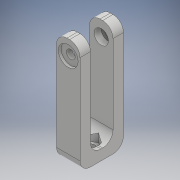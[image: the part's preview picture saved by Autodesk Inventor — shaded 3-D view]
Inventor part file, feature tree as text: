
AUTODESK INVENTOR PART (.ipt)
format: ipt  version: 2019 (Build 230136000, 136)  size: 224,768 bytes
history: native  units: mm
features: extrude x10, sketch x10, fillet x3, other x1, projected_geometry x1
ambient origin geometry x8: Origin, YZ Plane, XZ Plane, XY Plane, X Axis, Y Axis, Z Axis, Center Point
bodies: Body1 (feature_tree)
feature tree (25):
  other  "Sólido1"
  extrude  "Extrusión1"  Depth=6.0mm TaperAngle=0.0deg
  extrude  "Extrusión2"  Depth=115.0mm TaperAngle=0.0deg
  extrude  "Extrusión3"  Depth=17.0mm
  extrude  "Extrusión4"  Depth=27.0mm
  extrude  "Extrusión8"  Depth=12.0mm
  extrude  "Extrusión9"  Depth=10.0mm TaperAngle=0.0deg
  extrude  "Extrusión10"  Depth=2.5mm TaperAngle=0.0deg
  extrude  "Extrusión11"  Depth=3.0mm TaperAngle=0.0deg
  extrude  "Extrusión12"  Depth=8.0mm
  extrude  "Extrusión13"  Depth=12.0mm
  fillet  "Empalme4"  Radius=8.0mm
  fillet  "Empalme5"  Radius=16.0mm
  fillet  "Empalme6"  Radius=12.0mm
  sketch  "Boceto1"  dims[d0=6.0mm d1=0.0mm d2=6.0mm d3=0.0mm]
  sketch  "Boceto2"  dims[d5=3.0mm d6=0.0mm d7=115.0mm d8=0.0mm]
  projected_geometry  "Contorno proyectado1"
  sketch  "Boceto3"  dims[d18=11.0mm d20=17.0mm]
  sketch  "Boceto5"  dims[d21=5.0mm d22=27.0mm]
  sketch  "Boceto9"  dims[d23=50.0mm d24=12.0mm]
  sketch  "Boceto10"  dims[d25=10.0mm d26=10.0mm d27=0.0mm]
  sketch  "Boceto11"  dims[d29=22.0mm d30=2.5mm d31=0.0mm]
  sketch  "Boceto12"  dims[d32=12.0mm d34=3.0mm d35=0.0mm]
  sketch  "Boceto14"  dims[d36=3.0mm d37=0.0mm d38=8.0mm]
  sketch  "Boceto15"  dims[d39=3.0mm d40=0.0mm d41=16.5mm d42=8.0mm d43=0.0mm d45=16.0mm d46=12.0mm d47=12.0mm d48=12.0mm]
